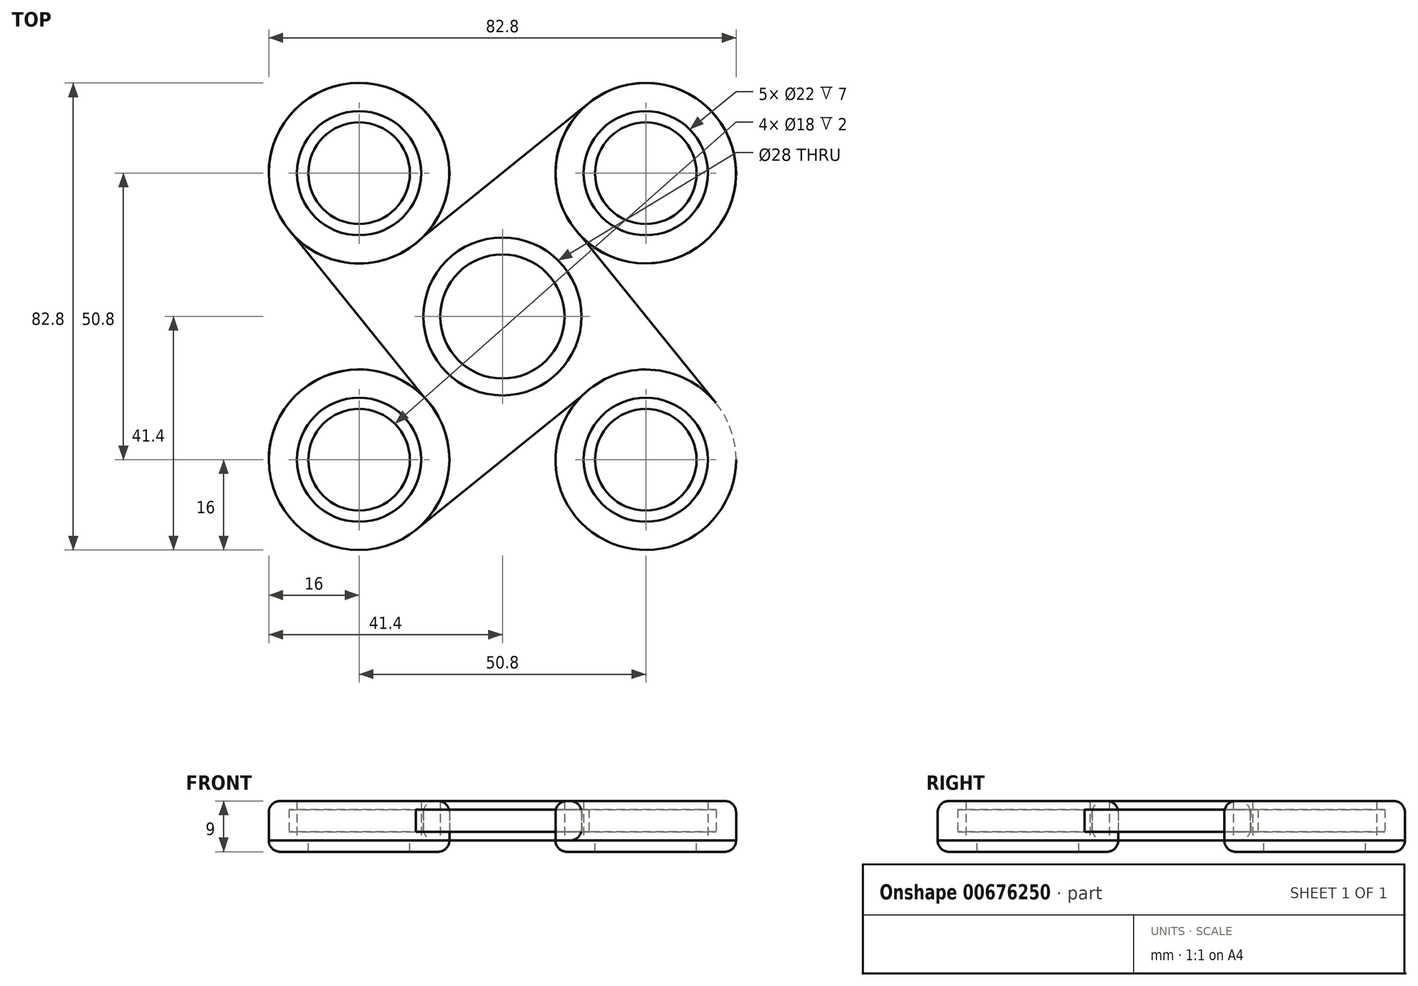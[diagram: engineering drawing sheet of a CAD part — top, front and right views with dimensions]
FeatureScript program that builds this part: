
annotation { "Feature Type Name" : "Feature", "Feature Type Description" : "" }
export const myFeature = defineFeature(function(context is Context, id is Id, definition is map)
    precondition{}
    {
        {
            var Q0;
            Q0=qCreatedBy(makeId("Top.planeOp"),FACE);
            var sketch = newSketch(context, id + "F0", { "sketchPlane" : qUnion([Q0])});
            skLineSegment(sketch, "E0.bottom", {"start": v(0, 0) * mm, "end": v(50.8, 0) * mm, "construction": true});
            skLineSegment(sketch, "E0.top", {"start": v(0, -50.8) * mm, "end": v(50.8, -50.8) * mm, "construction": true});
            skLineSegment(sketch, "E0.left", {"start": v(0, 0) * mm, "end": v(0, -50.8) * mm, "construction": true});
            skLineSegment(sketch, "E0.right", {"start": v(50.8, 0) * mm, "end": v(50.8, -50.8) * mm, "construction": true});
            skCircle(sketch, "E1", {"center": v(0, 0) * mm, "radius": 11 * mm});
            skCircle(sketch, "E2", {"center": v(50.8, 0) * mm, "radius": 11 * mm});
            skCircle(sketch, "E3", {"center": v(50.8, -50.8) * mm, "radius": 11 * mm});
            skCircle(sketch, "E4", {"center": v(0, -50.8) * mm, "radius": 11 * mm});
            skCircle(sketch, "E5", {"center": v(0, -50.8) * mm, "radius": 4 * mm});
            skCircle(sketch, "E6", {"center": v(0, 0) * mm, "radius": 4 * mm});
            skCircle(sketch, "E7", {"center": v(50.8, 0) * mm, "radius": 4 * mm});
            skCircle(sketch, "E8", {"center": v(50.8, -50.8) * mm, "radius": 4 * mm});
            skLineSegment(sketch, "E9", {"start": v(0, -50.8) * mm, "end": v(50.8, 0) * mm, "construction": true});
            skLineSegment(sketch, "E10", {"start": v(50.8, -50.8) * mm, "end": v(0, 0) * mm, "construction": true});
            skCircle(sketch, "E11", {"center": v(25.4, -25.4) * mm, "radius": 4 * mm});
            skCircle(sketch, "E12", {"center": v(25.4, -25.4) * mm, "radius": 11 * mm});
            skCircle(sketch, "E13", {"center": v(0, 0) * mm, "radius": 16 * mm});
            skCircle(sketch, "E14", {"center": v(50.8, 0) * mm, "radius": 16 * mm});
            skCircle(sketch, "E15", {"center": v(50.8, -50.8) * mm, "radius": 16 * mm});
            skCircle(sketch, "E16", {"center": v(0, -50.8) * mm, "radius": 16 * mm});
            skLineSegment(sketch, "E17", {"start": v(11.31, -11.31) * mm, "end": v(40.75, 12.45) * mm});
            skLineSegment(sketch, "E18", {"start": v(40.75, 12.45) * mm, "end": v(50.8, 0) * mm});
            skLineSegment(sketch, "E19", {"start": v(39.49, -11.31) * mm, "end": v(63.25, -40.75) * mm});
            skLineSegment(sketch, "E20", {"start": v(63.25, -40.75) * mm, "end": v(50.8, -50.8) * mm});
            skLineSegment(sketch, "E21", {"start": v(39.49, -39.49) * mm, "end": v(10.05, -63.25) * mm});
            skLineSegment(sketch, "E22", {"start": v(10.05, -63.25) * mm, "end": v(0, -50.8) * mm});
            skLineSegment(sketch, "E23", {"start": v(11.31, -39.49) * mm, "end": v(-12.45, -10.05) * mm});
            skLineSegment(sketch, "E24", {"start": v(-12.45, -10.05) * mm, "end": v(0, 0) * mm});
            skCircle(sketch, "E25", {"center": v(25.4, -25.4) * mm, "radius": 14 * mm});
            skSolve(sketch);
        }
        {
            var Q0;
            {var subQ5=sQuery(id+"F0.wireOp",EDGE,"E17");Q0=makeQuery(id+"F0.imprint","IMPRINT",FACE,{"disambiguationData":[TD([[makeQuery(id+"F0.imprint","IMPRINT",EDGE,{"derivedFrom":subQ5}),-1.0]])]});}
            extrude(context, id + "F1", {"entities" : qUnion([Q0]), "endBound" : BoundingType.SYMMETRIC, "depth" : 4 * mm, "offsetDistance" : 25 * mm});
        }
        {
            var Q0;
            Q0=makeQuery(id+"F0.imprint","IMPRINT",FACE,{"disambiguationData":[TD([[makeQuery(id+"F0.imprint","IMPRINT",EDGE,{"derivedFrom":sQuery(id+"F0.wireOp",EDGE,"E4")}),-1.0]])]});
            var Q1;
            Q1=makeQuery(id+"F0.imprint","IMPRINT",FACE,{"disambiguationData":[TD([[makeQuery(id+"F0.imprint","IMPRINT",EDGE,{"derivedFrom":sQuery(id+"F0.wireOp",EDGE,"E3")}),-1.0]])]});
            var Q2;
            Q2=makeQuery(id+"F0.imprint","IMPRINT",FACE,{"disambiguationData":[TD([[makeQuery(id+"F0.imprint","IMPRINT",EDGE,{"derivedFrom":sQuery(id+"F0.wireOp",EDGE,"E2")}),-1.0]])]});
            var Q3;
            Q3=makeQuery(id+"F0.imprint","IMPRINT",FACE,{"disambiguationData":[TD([[makeQuery(id+"F0.imprint","IMPRINT",EDGE,{"derivedFrom":sQuery(id+"F0.wireOp",EDGE,"E1")}),-1.0]])]});
            extrude(context, id + "F2", {"entities" : qUnion([Q0, Q1, Q2, Q3]), "endBound" : BoundingType.SYMMETRIC, "depth" : 7 * mm, "offsetDistance" : 25 * mm});
        }
        {
            var Q0;
            Q0=makeQuery(id+"F2.opExtrude","CAP_FACE",FACE,{"disambiguationData":[OSD([sQuery(id+"F0.wireOp",EDGE,"E4"),sQuery(id+"F0.wireOp",EDGE,"E16")])],"isStart":true});
            var sketch = newSketch(context, id + "F3", { "sketchPlane" : qUnion([Q0])});
            skCircle(sketch, "E26.0", {"center": v(0, 50.8) * mm, "radius": 16 * mm});
            skCircle(sketch, "E26.1", {"center": v(50.8, 50.8) * mm, "radius": 16 * mm});
            skCircle(sketch, "E26.2", {"center": v(50.8, 0) * mm, "radius": 16 * mm});
            skCircle(sketch, "E26.3", {"center": v(0, 0) * mm, "radius": 16 * mm});
            skCircle(sketch, "E27", {"center": v(0, 50.8) * mm, "radius": 9 * mm});
            skCircle(sketch, "E28", {"center": v(50.8, 50.8) * mm, "radius": 9 * mm});
            skCircle(sketch, "E29", {"center": v(50.8, 0) * mm, "radius": 9 * mm});
            skCircle(sketch, "E30", {"center": v(0, 0) * mm, "radius": 9 * mm});
            skSolve(sketch);
        }
        {
            var Q0;
            Q0=makeQuery(id+"F3.imprint","IMPRINT",FACE,{"disambiguationData":[TD([[makeQuery(id+"F3.imprint","IMPRINT",EDGE,{"derivedFrom":sQuery(id+"F3.wireOp",EDGE,"E27")}),-1.0]])]});
            var Q1;
            Q1=makeQuery(id+"F3.imprint","IMPRINT",FACE,{"disambiguationData":[TD([[makeQuery(id+"F3.imprint","IMPRINT",EDGE,{"derivedFrom":sQuery(id+"F3.wireOp",EDGE,"E26.0")}),-1.0]])]});
            var Q2;
            Q2=makeQuery(id+"F3.imprint","IMPRINT",FACE,{"disambiguationData":[TD([[makeQuery(id+"F3.imprint","IMPRINT",EDGE,{"derivedFrom":sQuery(id+"F3.wireOp",EDGE,"E26.1")}),1.0]])]});
            var Q3;
            Q3=makeQuery(id+"F3.imprint","IMPRINT",FACE,{"disambiguationData":[TD([[makeQuery(id+"F3.imprint","IMPRINT",EDGE,{"derivedFrom":sQuery(id+"F3.wireOp",EDGE,"E26.2")}),1.0]])]});
            var Q4;
            Q4=makeQuery(id+"F3.imprint","IMPRINT",FACE,{"disambiguationData":[TD([[makeQuery(id+"F3.imprint","IMPRINT",EDGE,{"derivedFrom":sQuery(id+"F3.wireOp",EDGE,"E26.3")}),1.0]])]});
            extrude(context, id + "F4", {"entities" : qUnion([Q0, Q1, Q2, Q3, Q4]), "depth" : 2 * mm, "offsetDistance" : 25 * mm});
        }
        {
            var Q0;
            Q0=makeQuery(id+"F0.imprint","IMPRINT",FACE,{"disambiguationData":[TD([[makeQuery(id+"F0.imprint","IMPRINT",EDGE,{"derivedFrom":sQuery(id+"F0.wireOp",EDGE,"E12")}),-1.0]])]});
            extrude(context, id + "F5", {"entities" : qUnion([Q0]), "endBound" : BoundingType.SYMMETRIC, "depth" : 7 * mm, "offsetDistance" : 25 * mm});
        }
        {
            var Q0;
            Q0=makeQuery(id+"F2.opExtrude","CAP_EDGE",EDGE,{"disambiguationData":[OSD([sQuery(id+"F0.wireOp",EDGE,"E16")])],"isStart":false});
            var Q1;
            Q1=makeQuery(id+"F4.opExtrude","CAP_EDGE",EDGE,{"disambiguationData":[OSD([sQuery(id+"F3.wireOp",EDGE,"E26.0")])],"isStart":false});
            var Q2;
            Q2=makeQuery(id+"F4.opExtrude","CAP_EDGE",EDGE,{"disambiguationData":[OSD([sQuery(id+"F3.wireOp",EDGE,"E26.1")])],"isStart":false});
            var Q3;
            Q3=makeQuery(id+"F2.opExtrude","CAP_EDGE",EDGE,{"disambiguationData":[OSD([sQuery(id+"F0.wireOp",EDGE,"E15")])],"isStart":false});
            var Q4;
            Q4=makeQuery(id+"F4.opExtrude","CAP_EDGE",EDGE,{"disambiguationData":[OSD([sQuery(id+"F3.wireOp",EDGE,"E26.2")])],"isStart":false});
            var Q5;
            Q5=makeQuery(id+"F2.opExtrude","CAP_EDGE",EDGE,{"disambiguationData":[OSD([sQuery(id+"F0.wireOp",EDGE,"E14")])],"isStart":false});
            var Q6;
            Q6=makeQuery(id+"F4.opExtrude","CAP_EDGE",EDGE,{"disambiguationData":[OSD([sQuery(id+"F3.wireOp",EDGE,"E26.3")])],"isStart":false});
            var Q7;
            Q7=makeQuery(id+"F2.opExtrude","CAP_EDGE",EDGE,{"disambiguationData":[OSD([sQuery(id+"F0.wireOp",EDGE,"E13")])],"isStart":false});
            var Q8;
            Q8=makeQuery(id+"F5.opExtrude","CAP_EDGE",EDGE,{"disambiguationData":[OSD([sQuery(id+"F0.wireOp",EDGE,"E25")])],"isStart":false});
            var Q9;
            Q9=makeQuery(id+"F5.opExtrude","CAP_EDGE",EDGE,{"disambiguationData":[OSD([sQuery(id+"F0.wireOp",EDGE,"E25")])],"isStart":true});
            fillet(context, id + "F6", {"entities" : qUnion([Q0, Q1, Q2, Q3, Q4, Q5, Q6, Q7, Q8, Q9]), "radius" : 2 * mm, "tangentPropagation" : true, "allowEdgeOverflow" : false});
        }
    });
